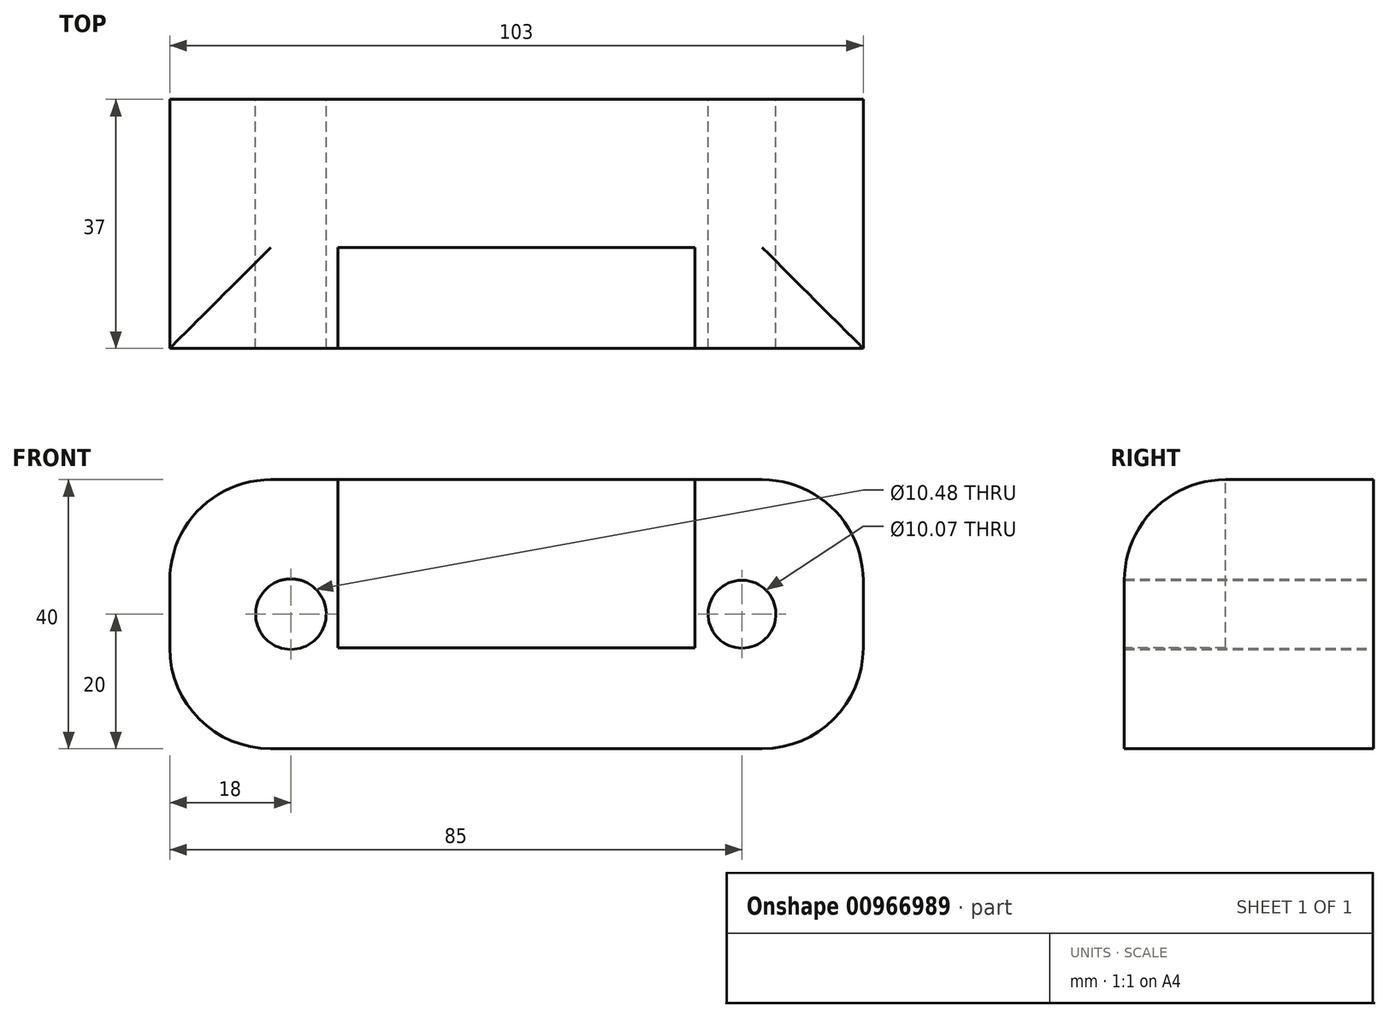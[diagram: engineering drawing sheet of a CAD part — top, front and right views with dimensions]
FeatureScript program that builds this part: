
annotation { "Feature Type Name" : "Feature", "Feature Type Description" : "" }
export const myFeature = defineFeature(function(context is Context, id is Id, definition is map)
    precondition{}
    {
        {
            var Q0;
            Q0=qCreatedBy(makeId("Front.planeOp"),FACE);
            var sketch = newSketch(context, id + "F0", { "sketchPlane" : qUnion([Q0])});
            skLineSegment(sketch, "E0.bottom", {"start": v(51.5, 20) * mm, "end": v(-51.5, 20) * mm});
            skLineSegment(sketch, "E0.top", {"start": v(51.5, -20) * mm, "end": v(-51.5, -20) * mm});
            skLineSegment(sketch, "E0.left", {"start": v(51.5, 20) * mm, "end": v(51.5, -20) * mm});
            skLineSegment(sketch, "E0.right", {"start": v(-51.5, 20) * mm, "end": v(-51.5, -20) * mm});
            skPoint(sketch, "E0.middle", {"position": v(0, 0) * mm});
            skCircle(sketch, "E1", {"center": v(-33.5, 0) * mm, "radius": 5.24 * mm});
            skCircle(sketch, "E2", {"center": v(33.5, 0) * mm, "radius": 5.04 * mm});
            skSolve(sketch);
        }
        {
            var Q0;
            Q0 = qSketchRegion(id + "F0", true);
            extrude(context, id + "F1", {"entities" : qUnion([Q0]), "depth" : 37 * mm, "offsetDistance" : 25 * mm});
        }
        {
            var Q0;
            Q0=makeQuery(id+"F1.opExtrude","SWEPT_EDGE",EDGE,{"disambiguationData":[OSD([sQuery(id+"F0.wireOp",EDGE,"E0.bottom"),sQuery(id+"F0.wireOp",EDGE,"E0.left")])]});
            var Q1;
            Q1=makeQuery(id+"F1.opExtrude","SWEPT_EDGE",EDGE,{"disambiguationData":[OSD([sQuery(id+"F0.wireOp",EDGE,"E0.bottom"),sQuery(id+"F0.wireOp",EDGE,"E0.right")])]});
            var Q2;
            Q2=makeQuery(id+"F1.opExtrude","SWEPT_EDGE",EDGE,{"disambiguationData":[OSD([sQuery(id+"F0.wireOp",EDGE,"E0.top"),sQuery(id+"F0.wireOp",EDGE,"E0.left")])]});
            var Q3;
            Q3=makeQuery(id+"F1.opExtrude","SWEPT_EDGE",EDGE,{"disambiguationData":[OSD([sQuery(id+"F0.wireOp",EDGE,"E0.top"),sQuery(id+"F0.wireOp",EDGE,"E0.right")])]});
            var Q4;
            Q4=makeQuery(id+"F1.opExtrude","CAP_EDGE",EDGE,{"disambiguationData":[OSD([sQuery(id+"F0.wireOp",EDGE,"E0.bottom")])],"isStart":false});
            fillet(context, id + "F2", {"entities" : qUnion([Q0, Q1, Q2, Q3, Q4]), "radius" : 15 * mm, "tangentPropagation" : true, "allowEdgeOverflow" : false});
        }
        {
            var Q0;
            Q0=makeQuery(id+"F1.opExtrude","SWEPT_FACE",FACE,{"disambiguationData":[OSD([sQuery(id+"F0.wireOp",EDGE,"E0.bottom")])]});
            var sketch = newSketch(context, id + "F3", { "sketchPlane" : qUnion([Q0])});
            skLineSegment(sketch, "E3.bottom", {"start": v(-26.5, -22) * mm, "end": v(26.5, -22) * mm});
            skLineSegment(sketch, "E3.top", {"start": v(-26.5, -45.47) * mm, "end": v(26.5, -45.47) * mm});
            skLineSegment(sketch, "E3.left", {"start": v(-26.5, -22) * mm, "end": v(-26.5, -45.47) * mm});
            skLineSegment(sketch, "E3.right", {"start": v(26.5, -22) * mm, "end": v(26.5, -45.47) * mm});
            skSolve(sketch);
        }
        {
            var Q0;
            Q0 = qSketchRegion(id + "F3", true);
            extrude(context, id + "F4", {"entities" : qUnion([Q0]), "operationType" : NewBodyOperationType.REMOVE, "oppositeDirection" : true, "depth" : 25 * mm, "offsetDistance" : 25 * mm});
        }
    });
